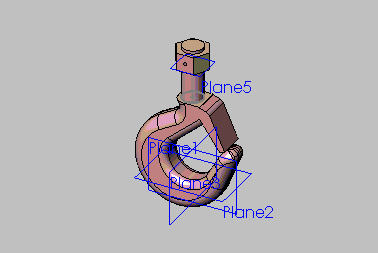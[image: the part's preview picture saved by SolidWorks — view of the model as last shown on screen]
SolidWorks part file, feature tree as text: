
SOLIDWORKS PART (.sldprt)
format: sldprt  version: not decoded by parser v0  size: 672,256 bytes
history: native  units: mm
features: plane x5, sketch x4, extrude x3, fillet x2, material x1, mirror x1, cut_extrude x1 (+10 scaffold rows collapsed)
feature tree (27):
  scaffold x10  (default folders/planes/origin — collapsed)
  material  "Material <not specified>"
  plane  "Plane1"  Offset=0mm
  plane  "Plane2"  Offset=0mm
  plane  "Plane3"  Offset=0mm
  sketch  "Sketch1"
  extrude  "Extrude1"  Depth=23.8125mm
  fillet  "Fillet1"  Radius=19.05mm
  fillet  "Fillet2"  Radius=11.90625mm
  mirror  "Mirror1"
  sketch  "Sketch2"  dims[D1=38.1mm]
  extrude  "Extrude2"  Depth=98.425mm
  plane  "Plane4"  Offset=0mm
  plane  "Plane5"  Offset=60.325mm
  sketch  "Sketch3"  dims[D1=53.975mm]
  extrude  "Extrude3"  Depth=32.54375mm
  sketch  "Sketch4"  dims[D1=6.35mm D2=~16.271875mm]
  cut_extrude  "Cut-Extrude2"  [1 undecoded]
decode coverage: 8 of 11 modeling features carry decoded parameters
note: ~ marks probable driven/reference dimensions
note: 1 parameter value undecoded
note: suppression state not decoded; provenance and decode notes live in map.json
